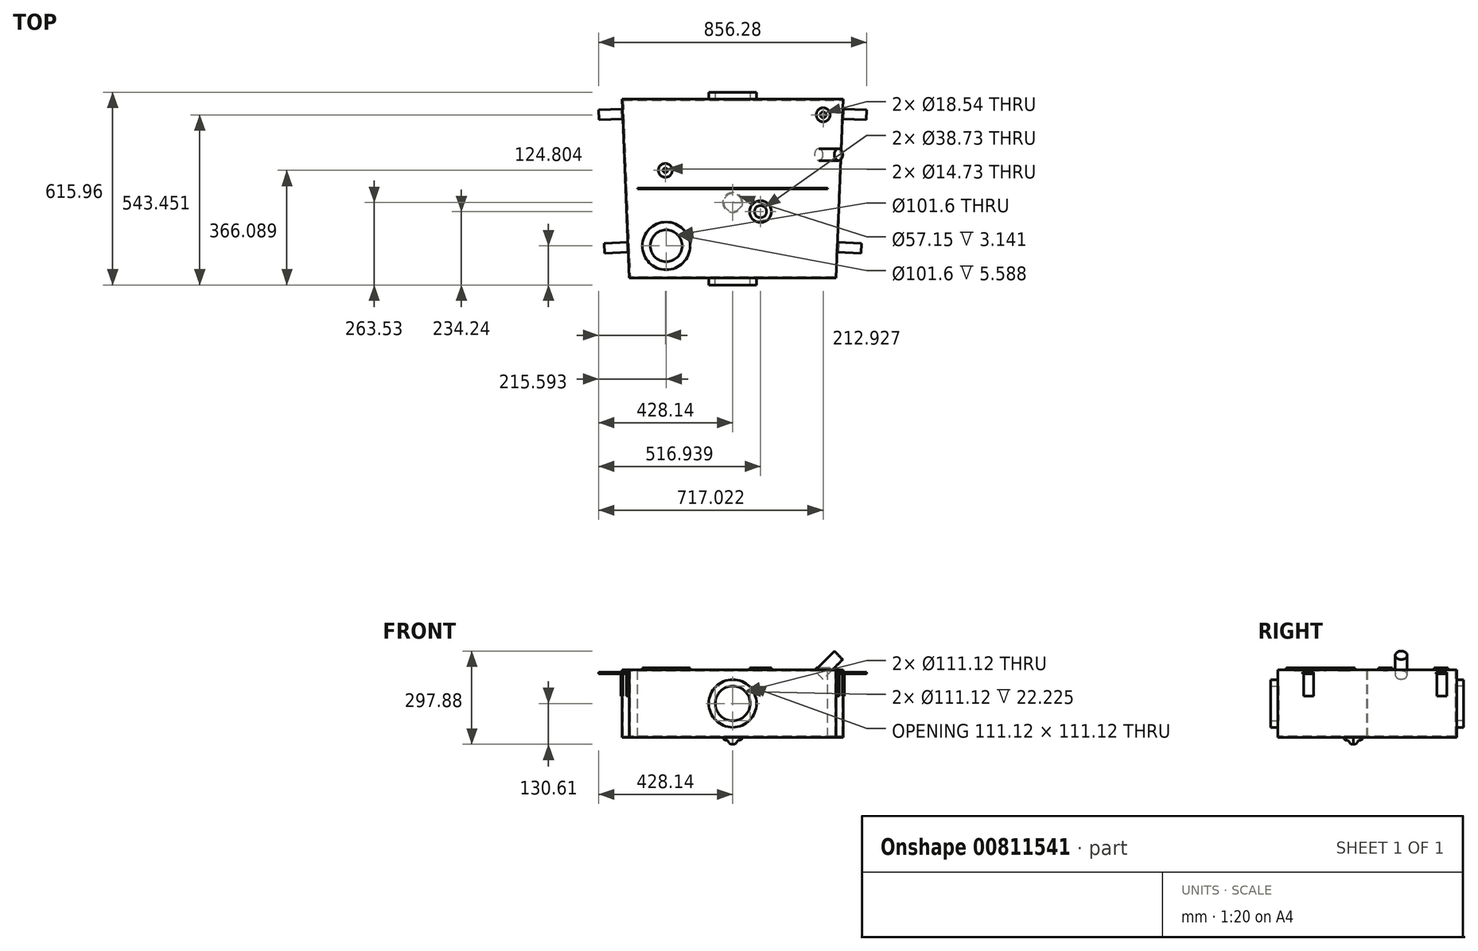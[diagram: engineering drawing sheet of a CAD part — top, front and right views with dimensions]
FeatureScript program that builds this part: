
annotation { "Feature Type Name" : "Feature", "Feature Type Description" : "" }
export const myFeature = defineFeature(function(context is Context, id is Id, definition is map)
    precondition{}
    {
        {
            var Q0;
            Q0=qCreatedBy(makeId("Top.planeOp"),FACE);
            var sketch = newSketch(context, id + "F0", { "sketchPlane" : qUnion([Q0])});
            skCircle(sketch, "E0", {"center": v(299.82, -177.22) * mm, "radius": 19.05 * mm});
            skCircle(sketch, "E1", {"center": v(288.88, -50.28) * mm, "radius": 9.27 * mm});
            skCircle(sketch, "E2", {"center": v(88.8, -359.5) * mm, "radius": 19.37 * mm});
            skCircle(sketch, "E3", {"center": v(88.8, -359.5) * mm, "radius": 34.93 * mm});
            skCircle(sketch, "E4", {"center": v(-212.55, -468.93) * mm, "radius": 76.2 * mm});
            skCircle(sketch, "E5", {"center": v(-212.55, -468.93) * mm, "radius": 50.8 * mm});
            skCircle(sketch, "E6", {"center": v(-215.21, -227.64) * mm, "radius": 22.23 * mm});
            skCircle(sketch, "E7", {"center": v(-215.21, -227.64) * mm, "radius": 7.37 * mm});
            skCircle(sketch, "E8", {"center": v(288.88, -50.28) * mm, "radius": 22.23 * mm});
            skLineSegment(sketch, "E9", {"start": v(0, -571.5) * mm, "end": v(330.2, -571.5) * mm});
            skLineSegment(sketch, "E10", {"start": v(0, 0) * mm, "end": v(353.29, 0) * mm});
            skLineSegment(sketch, "E11", {"start": v(353.29, 0) * mm, "end": v(330.2, -571.5) * mm});
            skLineSegment(sketch, "E12", {"start": v(356.77, -31.92) * mm, "end": v(352, -31.72) * mm});
            skLineSegment(sketch, "E13", {"start": v(356.77, -31.92) * mm, "end": v(355.48, -63.64) * mm});
            skLineSegment(sketch, "E14", {"start": v(355.48, -63.64) * mm, "end": v(350.73, -63.45) * mm});
            skLineSegment(sketch, "E15", {"start": v(338.3, -489.2) * mm, "end": v(333.53, -489.02) * mm});
            skLineSegment(sketch, "E16", {"start": v(338.3, -489.2) * mm, "end": v(339.57, -457.49) * mm});
            skLineSegment(sketch, "E17", {"start": v(339.57, -457.49) * mm, "end": v(334.81, -457.3) * mm});
            skLineSegment(sketch, "E18.MirrorCS", {"start": v(0, -571.5) * mm, "end": v(-330.2, -571.5) * mm});
            skLineSegment(sketch, "E19.MirrorCS", {"start": v(-353.29, 0) * mm, "end": v(-330.2, -571.5) * mm});
            skLineSegment(sketch, "E20.MirrorCS", {"start": v(0, 0) * mm, "end": v(-353.29, 0) * mm});
            skLineSegment(sketch, "E21.MirrorCS", {"start": v(-339.57, -457.49) * mm, "end": v(-334.81, -457.3) * mm});
            skLineSegment(sketch, "E22.MirrorCS", {"start": v(-338.3, -489.2) * mm, "end": v(-339.57, -457.49) * mm});
            skLineSegment(sketch, "E23.MirrorCS", {"start": v(-338.3, -489.2) * mm, "end": v(-333.53, -489.02) * mm});
            skLineSegment(sketch, "E24.MirrorCS", {"start": v(-356.77, -31.92) * mm, "end": v(-352, -31.72) * mm});
            skLineSegment(sketch, "E25.MirrorCS", {"start": v(-355.48, -63.64) * mm, "end": v(-350.73, -63.45) * mm});
            skLineSegment(sketch, "E26.MirrorCS", {"start": v(-356.77, -31.92) * mm, "end": v(-355.48, -63.64) * mm});
            skLineSegment(sketch, "E27", {"start": v(318.87, -177.28) * mm, "end": v(318.87, -145.64) * mm, "construction": true});
            skLineSegment(sketch, "E28", {"start": v(303.64, -284.16) * mm, "end": v(0, -284.16) * mm});
            skLineSegment(sketch, "E29", {"start": v(303.64, -287.34) * mm, "end": v(0, -287.34) * mm});
            skLineSegment(sketch, "E30", {"start": v(303.64, -284.16) * mm, "end": v(303.64, -287.34) * mm});
            skLineSegment(sketch, "E31.MirrorCS", {"start": v(-303.64, -284.16) * mm, "end": v(0, -284.16) * mm});
            skLineSegment(sketch, "E32.MirrorCS", {"start": v(-303.64, -287.34) * mm, "end": v(0, -287.34) * mm});
            skLineSegment(sketch, "E33.MirrorCS", {"start": v(-303.64, -284.16) * mm, "end": v(-303.64, -287.34) * mm});
            skLineSegment(sketch, "E34", {"start": v(318.87, -177.28) * mm, "end": v(280.77, -177.28) * mm, "construction": true});
            skLineSegment(sketch, "E35", {"start": v(-212.55, -468.93) * mm, "end": v(-215.21, -227.64) * mm, "construction": true});
            skSolve(sketch);
        }
        {
            var Q0;
            Q0=makeQuery(id+"F0.imprint","IMPRINT",FACE,{"disambiguationData":[TD([[makeQuery(id+"F0.imprint","IMPRINT",EDGE,{"derivedFrom":sQuery(id+"F0.wireOp",EDGE,"E0")}),-1.0]])]});
            var Q1;
            Q1=makeQuery(id+"F0.imprint","IMPRINT",FACE,{"disambiguationData":[TD([[makeQuery(id+"F0.imprint","IMPRINT",EDGE,{"derivedFrom":sQuery(id+"F0.wireOp",EDGE,"E6")}),1.0]])]});
            var Q2;
            Q2=makeQuery(id+"F0.imprint","IMPRINT",FACE,{"disambiguationData":[TD([[makeQuery(id+"F0.imprint","IMPRINT",EDGE,{"derivedFrom":sQuery(id+"F0.wireOp",EDGE,"E7")}),1.0]])]});
            var Q3;
            Q3=makeQuery(id+"F0.imprint","IMPRINT",FACE,{"disambiguationData":[TD([[makeQuery(id+"F0.imprint","IMPRINT",EDGE,{"derivedFrom":sQuery(id+"F0.wireOp",EDGE,"E4")}),1.0]])]});
            var Q4;
            Q4=makeQuery(id+"F0.imprint","IMPRINT",FACE,{"disambiguationData":[TD([[makeQuery(id+"F0.imprint","IMPRINT",EDGE,{"derivedFrom":sQuery(id+"F0.wireOp",EDGE,"E5")}),1.0]])]});
            var Q5;
            Q5=makeQuery(id+"F0.imprint","IMPRINT",FACE,{"disambiguationData":[TD([[makeQuery(id+"F0.imprint","IMPRINT",EDGE,{"derivedFrom":sQuery(id+"F0.wireOp",EDGE,"E28")}),1.0]])]});
            var Q6;
            Q6=makeQuery(id+"F0.imprint","IMPRINT",FACE,{"disambiguationData":[TD([[makeQuery(id+"F0.imprint","IMPRINT",EDGE,{"derivedFrom":sQuery(id+"F0.wireOp",EDGE,"E2")}),-1.0]])]});
            var Q7;
            Q7=makeQuery(id+"F0.imprint","IMPRINT",FACE,{"disambiguationData":[TD([[makeQuery(id+"F0.imprint","IMPRINT",EDGE,{"derivedFrom":sQuery(id+"F0.wireOp",EDGE,"E2")}),1.0]])]});
            var Q8;
            Q8=makeQuery(id+"F0.imprint","IMPRINT",FACE,{"disambiguationData":[TD([[makeQuery(id+"F0.imprint","IMPRINT",EDGE,{"derivedFrom":sQuery(id+"F0.wireOp",EDGE,"E0")}),1.0]])]});
            var Q9;
            Q9=makeQuery(id+"F0.imprint","IMPRINT",FACE,{"disambiguationData":[TD([[makeQuery(id+"F0.imprint","IMPRINT",EDGE,{"derivedFrom":sQuery(id+"F0.wireOp",EDGE,"E1")}),-1.0]])]});
            var Q10;
            Q10=makeQuery(id+"F0.imprint","IMPRINT",FACE,{"disambiguationData":[TD([[makeQuery(id+"F0.imprint","IMPRINT",EDGE,{"derivedFrom":sQuery(id+"F0.wireOp",EDGE,"E1")}),1.0]])]});
            extrude(context, id + "F1", {"entities" : qUnion([Q0, Q1, Q2, Q3, Q4, Q5, Q6, Q7, Q8, Q9, Q10]), "oppositeDirection" : true, "depth" : 215.9 * mm, "offsetDistance" : 25.4 * mm});
        }
        {
            var Q0;
            Q0=makeQuery(id+"F1.opExtrude","CAP_FACE",FACE,{"disambiguationData":[OSD([sQuery(id+"F0.wireOp",EDGE,"E9"),sQuery(id+"F0.wireOp",EDGE,"E10"),sQuery(id+"F0.wireOp",EDGE,"E11"),sQuery(id+"F0.wireOp",EDGE,"E18.MirrorCS"),sQuery(id+"F0.wireOp",EDGE,"E19.MirrorCS"),sQuery(id+"F0.wireOp",EDGE,"E20.MirrorCS")])],"isStart":true});
            var Q1;
            Q1=makeQuery(id+"F1.opExtrude","SWEPT_BODY",BODY,{"disambiguationData":[OSD([sQuery(id+"F0.wireOp",EDGE,"E9"),sQuery(id+"F0.wireOp",EDGE,"E10"),sQuery(id+"F0.wireOp",EDGE,"E11"),sQuery(id+"F0.wireOp",EDGE,"E18.MirrorCS"),sQuery(id+"F0.wireOp",EDGE,"E19.MirrorCS"),sQuery(id+"F0.wireOp",EDGE,"E20.MirrorCS")])]});
            shell(context, id + "F2", {"isHollow" : true, "entities" : qUnion([Q0]), "parts" : qUnion([Q1]), "thickness" : 3.17 * mm});
        }
        {
            var Q0;
            Q0=makeQuery(id+"F0.imprint","IMPRINT",FACE,{"disambiguationData":[TD([[makeQuery(id+"F0.imprint","IMPRINT",EDGE,{"derivedFrom":sQuery(id+"F0.wireOp",EDGE,"E28")}),1.0]])]});
            extrude(context, id + "F3", {"entities" : qUnion([Q0]), "oppositeDirection" : true, "depth" : 215.9 * mm, "offsetDistance" : 25.4 * mm});
        }
        {
            var Q0;
            Q0=makeQuery(id+"F0.imprint","IMPRINT",FACE,{"disambiguationData":[TD([[makeQuery(id+"F0.imprint","IMPRINT",EDGE,{"derivedFrom":sQuery(id+"F0.wireOp",EDGE,"E7")}),1.0]])]});
            var Q1;
            Q1=makeQuery(id+"F0.imprint","IMPRINT",FACE,{"disambiguationData":[TD([[makeQuery(id+"F0.imprint","IMPRINT",EDGE,{"derivedFrom":sQuery(id+"F0.wireOp",EDGE,"E5")}),1.0]])]});
            var Q2;
            Q2=makeQuery(id+"F0.imprint","IMPRINT",FACE,{"disambiguationData":[TD([[makeQuery(id+"F0.imprint","IMPRINT",EDGE,{"derivedFrom":sQuery(id+"F0.wireOp",EDGE,"E2")}),1.0]])]});
            var Q3;
            Q3=makeQuery(id+"F0.imprint","IMPRINT",FACE,{"disambiguationData":[TD([[makeQuery(id+"F0.imprint","IMPRINT",EDGE,{"derivedFrom":sQuery(id+"F0.wireOp",EDGE,"E1")}),1.0]])]});
            extrude(context, id + "F4", {"entities" : qUnion([Q0, Q1, Q2, Q3]), "operationType" : NewBodyOperationType.REMOVE, "oppositeDirection" : true, "depth" : 3.3 * mm, "offsetDistance" : 25.4 * mm});
        }
        {
            var Q0;
            Q0=makeQuery(id+"F0.imprint","IMPRINT",FACE,{"disambiguationData":[TD([[makeQuery(id+"F0.imprint","IMPRINT",EDGE,{"derivedFrom":sQuery(id+"F0.wireOp",EDGE,"E6")}),1.0]])]});
            var Q1;
            Q1=makeQuery(id+"F0.imprint","IMPRINT",FACE,{"disambiguationData":[TD([[makeQuery(id+"F0.imprint","IMPRINT",EDGE,{"derivedFrom":sQuery(id+"F0.wireOp",EDGE,"E4")}),1.0]])]});
            var Q2;
            Q2=makeQuery(id+"F0.imprint","IMPRINT",FACE,{"disambiguationData":[TD([[makeQuery(id+"F0.imprint","IMPRINT",EDGE,{"derivedFrom":sQuery(id+"F0.wireOp",EDGE,"E2")}),-1.0]])]});
            var Q3;
            Q3=makeQuery(id+"F0.imprint","IMPRINT",FACE,{"disambiguationData":[TD([[makeQuery(id+"F0.imprint","IMPRINT",EDGE,{"derivedFrom":sQuery(id+"F0.wireOp",EDGE,"E1")}),-1.0]])]});
            extrude(context, id + "F5", {"entities" : qUnion([Q0, Q1, Q2, Q3]), "depth" : 5.6 * mm, "offsetDistance" : 25.4 * mm});
        }
        {
            var Q0;
            Q0=makeQuery(id+"F1.opExtrude","SWEPT_FACE",FACE,{"disambiguationData":[OSD([sQuery(id+"F0.wireOp",EDGE,"E9"),sQuery(id+"F0.wireOp",EDGE,"E18.MirrorCS")])]});
            var sketch = newSketch(context, id + "F6", { "sketchPlane" : qUnion([Q0])});
            skCircle(sketch, "E36", {"center": v(0, -107.95) * mm, "radius": 76.2 * mm});
            skCircle(sketch, "E37", {"center": v(0, -107.95) * mm, "radius": 55.56 * mm});
            skSolve(sketch);
        }
        {
            var Q0;
            Q0=makeQuery(id+"F6.imprint","IMPRINT",FACE,{"disambiguationData":[TD([[makeQuery(id+"F6.imprint","IMPRINT",EDGE,{"derivedFrom":sQuery(id+"F6.wireOp",EDGE,"E37")}),1.0]])]});
            extrude(context, id + "F7", {"entities" : qUnion([Q0]), "operationType" : NewBodyOperationType.REMOVE, "oppositeDirection" : true, "depth" : 3.3 * mm, "offsetDistance" : 25.4 * mm});
        }
        {
            var Q0;
            Q0=makeQuery(id+"F6.imprint","IMPRINT",FACE,{"disambiguationData":[TD([[makeQuery(id+"F6.imprint","IMPRINT",EDGE,{"derivedFrom":sQuery(id+"F6.wireOp",EDGE,"E36")}),1.0]])]});
            extrude(context, id + "F8", {"entities" : qUnion([Q0]), "depth" : 22.22 * mm, "offsetDistance" : 25.4 * mm});
        }
        {
            var Q0;
            Q0=makeQuery(id+"F1.opExtrude","SWEPT_FACE",FACE,{"disambiguationData":[OSD([sQuery(id+"F0.wireOp",EDGE,"E10"),sQuery(id+"F0.wireOp",EDGE,"E20.MirrorCS")])]});
            var sketch = newSketch(context, id + "F9", { "sketchPlane" : qUnion([Q0])});
            skCircle(sketch, "E38", {"center": v(0, -107.95) * mm, "radius": 76.2 * mm});
            skCircle(sketch, "E39", {"center": v(0, -107.95) * mm, "radius": 55.56 * mm});
            skSolve(sketch);
        }
        {
            var Q0;
            Q0=makeQuery(id+"F9.imprint","IMPRINT",FACE,{"disambiguationData":[TD([[makeQuery(id+"F9.imprint","IMPRINT",EDGE,{"derivedFrom":sQuery(id+"F9.wireOp",EDGE,"E39")}),1.0]])]});
            extrude(context, id + "F10", {"entities" : qUnion([Q0]), "operationType" : NewBodyOperationType.REMOVE, "oppositeDirection" : true, "depth" : 3.3 * mm, "offsetDistance" : 25.4 * mm});
        }
        {
            var Q0;
            Q0=makeQuery(id+"F9.imprint","IMPRINT",FACE,{"disambiguationData":[TD([[makeQuery(id+"F9.imprint","IMPRINT",EDGE,{"derivedFrom":sQuery(id+"F9.wireOp",EDGE,"E38")}),1.0]])]});
            extrude(context, id + "F11", {"entities" : qUnion([Q0]), "depth" : 22.22 * mm, "offsetDistance" : 25.4 * mm});
        }
        {
            var Q0;
            Q0=makeQuery(id+"F1.opExtrude","CAP_FACE",FACE,{"disambiguationData":[OSD([sQuery(id+"F0.wireOp",EDGE,"E9"),sQuery(id+"F0.wireOp",EDGE,"E10"),sQuery(id+"F0.wireOp",EDGE,"E11"),sQuery(id+"F0.wireOp",EDGE,"E18.MirrorCS"),sQuery(id+"F0.wireOp",EDGE,"E19.MirrorCS"),sQuery(id+"F0.wireOp",EDGE,"E20.MirrorCS")])],"isStart":false});
            var sketch = newSketch(context, id + "F12", { "sketchPlane" : qUnion([Q0])});
            skLineSegment(sketch, "E40", {"start": v(0, 0) * mm, "end": v(0, 330.2) * mm, "construction": true});
            skCircle(sketch, "E41", {"center": v(0, 330.2) * mm, "radius": 28.58 * mm});
            skCircle(sketch, "E42", {"center": v(0, 330.2) * mm, "radius": 31.75 * mm});
            skSolve(sketch);
        }
        {
            var Q0;
            Q0=makeQuery(id+"F12.imprint","IMPRINT",FACE,{"disambiguationData":[TD([[makeQuery(id+"F12.imprint","IMPRINT",EDGE,{"derivedFrom":sQuery(id+"F12.wireOp",EDGE,"E41")}),1.0]])]});
            extrude(context, id + "F13", {"entities" : qUnion([Q0]), "operationType" : NewBodyOperationType.REMOVE, "oppositeDirection" : true, "depth" : 3.3 * mm, "offsetDistance" : 25.4 * mm});
        }
        {
            var Q0;
            Q0=qCreatedBy(makeId("Front.planeOp"),FACE);
            cPlane(context, id + "F14", {"entities" : qUnion([Q0]), "cplaneType" : CPlaneType.OFFSET, "offset" : 330.2 * mm, "width" : 152.4 * mm, "height" : 152.4 * mm});
        }
        {
            var Q0;
            Q0=qCreatedBy(id+"F14.planeOp",FACE);
            var sketch = newSketch(context, id + "F15", { "sketchPlane" : qUnion([Q0])});
            skLineSegment(sketch, "E43", {"start": v(0, -215.87) * mm, "end": v(31.74, -215.87) * mm});
            skLineSegment(sketch, "E44", {"start": v(0, -215.87) * mm, "end": v(0, -238.1) * mm});
            skFitSpline(sketch, "E45", {"points": [v(0, -238.1) * mm, v(6.54, -238.1) * mm, v(12.33, -232.24) * mm, v(18.56, -225.83) * mm, v(25.6, -224.58) * mm, v(31.74, -215.87) * mm], "startDerivative": vector(38.6, -6.75) * mm, "endDerivative": vector(23.38, 49.2) * mm});
            skSolve(sketch);
        }
        {
            var Q0;
            Q0=makeQuery(id+"F15.imprint","IMPRINT",FACE,{"disambiguationData":[TD([[makeQuery(id+"F15.imprint","IMPRINT",EDGE,{"derivedFrom":sQuery(id+"F15.wireOp",EDGE,"E43")}),-1.0]])]});
            extrude(context, id + "F16", {"entities" : qUnion([Q0]), "depth" : 0.25 * mm, "offsetDistance" : 25.4 * mm});
        }
        {
            var Q0;
            Q0=makeQuery(id+"F16.opExtrude","CAP_FACE",FACE,{"disambiguationData":[OSD([sQuery(id+"F15.wireOp",EDGE,"E43"),sQuery(id+"F15.wireOp",EDGE,"E44"),sQuery(id+"F15.wireOp",EDGE,"E45")])],"isStart":false});
            var Q1;
            Q1=makeQuery(id+"F16.opExtrude","CAP_EDGE",EDGE,{"disambiguationData":[OSD([sQuery(id+"F15.wireOp",EDGE,"E44")])],"isStart":true});
            revolve(context, id + "F17", {"operationType" : NewBodyOperationType.ADD, "surfaceOperationType" : NewSurfaceOperationType.NEW, "entities" : qUnion([Q0]), "axis" : qUnion([Q1]), "revolveType" : RevolveType.FULL});
        }
        {
            var Q0;
            {var subQ0=sQuery(id+"F0.wireOp",EDGE,"E24.MirrorCS");Q0=makeQuery(id+"F0.imprint","IMPRINT",FACE,{"disambiguationData":[TD([[makeQuery(id+"F0.imprint","IMPRINT",EDGE,{"derivedFrom":subQ0}),-1.0]])]});}
            var Q1;
            {var subQ0=sQuery(id+"F0.wireOp",EDGE,"E12");Q1=makeQuery(id+"F0.imprint","IMPRINT",FACE,{"disambiguationData":[TD([[makeQuery(id+"F0.imprint","IMPRINT",EDGE,{"derivedFrom":subQ0}),1.0]])]});}
            var Q2;
            {var subQ0=sQuery(id+"F0.wireOp",EDGE,"E15");Q2=makeQuery(id+"F0.imprint","IMPRINT",FACE,{"disambiguationData":[TD([[makeQuery(id+"F0.imprint","IMPRINT",EDGE,{"derivedFrom":subQ0}),-1.0]])]});}
            var Q3;
            {var subQ0=sQuery(id+"F0.wireOp",EDGE,"E21.MirrorCS");Q3=makeQuery(id+"F0.imprint","IMPRINT",FACE,{"disambiguationData":[TD([[makeQuery(id+"F0.imprint","IMPRINT",EDGE,{"derivedFrom":subQ0}),-1.0]])]});}
            extrude(context, id + "F18", {"entities" : qUnion([Q0, Q1, Q2, Q3]), "oppositeDirection" : true, "depth" : 84.14 * mm, "offsetDistance" : 25.4 * mm});
        }
        {
            var Q0;
            {var subQ0=sQuery(id+"F0.wireOp",EDGE,"E24.MirrorCS");Q0=makeQuery(id+"F0.imprint","IMPRINT",FACE,{"disambiguationData":[TD([[makeQuery(id+"F0.imprint","IMPRINT",EDGE,{"derivedFrom":subQ0}),-1.0]])]});}
            var Q1;
            {var subQ0=sQuery(id+"F0.wireOp",EDGE,"E12");Q1=makeQuery(id+"F0.imprint","IMPRINT",FACE,{"disambiguationData":[TD([[makeQuery(id+"F0.imprint","IMPRINT",EDGE,{"derivedFrom":subQ0}),1.0]])]});}
            var Q2;
            {var subQ0=sQuery(id+"F0.wireOp",EDGE,"E15");Q2=makeQuery(id+"F0.imprint","IMPRINT",FACE,{"disambiguationData":[TD([[makeQuery(id+"F0.imprint","IMPRINT",EDGE,{"derivedFrom":subQ0}),-1.0]])]});}
            var Q3;
            {var subQ0=sQuery(id+"F0.wireOp",EDGE,"E21.MirrorCS");Q3=makeQuery(id+"F0.imprint","IMPRINT",FACE,{"disambiguationData":[TD([[makeQuery(id+"F0.imprint","IMPRINT",EDGE,{"derivedFrom":subQ0}),-1.0]])]});}
            extrude(context, id + "F19", {"entities" : qUnion([Q0, Q1, Q2, Q3]), "operationType" : NewBodyOperationType.REMOVE, "oppositeDirection" : true, "depth" : 7.94 * mm, "offsetDistance" : 25.4 * mm});
        }
        {
            var Q0;
            Q0=makeQuery(id+"F18.opExtrude","SWEPT_FACE",FACE,{"disambiguationData":[OSD([sQuery(id+"F0.wireOp",EDGE,"E26.MirrorCS")])]});
            var sketch = newSketch(context, id + "F20", { "sketchPlane" : qUnion([Q0])});
            skLineSegment(sketch, "E46", {"start": v(17.49, -7.94) * mm, "end": v(17.49, -12.7) * mm});
            skLineSegment(sketch, "E47", {"start": v(17.49, -12.7) * mm, "end": v(49.24, -12.7) * mm});
            skLineSegment(sketch, "E48", {"start": v(49.24, -12.7) * mm, "end": v(49.24, -7.94) * mm});
            skLineSegment(sketch, "E49", {"start": v(49.24, -7.94) * mm, "end": v(17.49, -7.94) * mm});
            skSolve(sketch);
        }
        {
            var Q0;
            Q0=makeQuery(id+"F20.imprint","IMPRINT",FACE,{"disambiguationData":[TD([[makeQuery(id+"F20.imprint","IMPRINT",EDGE,{"derivedFrom":sQuery(id+"F20.wireOp",EDGE,"E46")}),-1.0]])]});
            extrude(context, id + "F21", {"entities" : qUnion([Q0]), "operationType" : NewBodyOperationType.ADD, "depth" : 71.44 * mm, "offsetDistance" : 25.4 * mm});
        }
        {
            var Q0;
            Q0=makeQuery(id+"F18.opExtrude","SWEPT_FACE",FACE,{"disambiguationData":[OSD([sQuery(id+"F0.wireOp",EDGE,"E22.MirrorCS")])]});
            var sketch = newSketch(context, id + "F22", { "sketchPlane" : qUnion([Q0])});
            skLineSegment(sketch, "E50", {"start": v(443.4, -7.94) * mm, "end": v(443.4, -12.7) * mm});
            skLineSegment(sketch, "E51", {"start": v(443.4, -12.7) * mm, "end": v(475.15, -12.7) * mm});
            skLineSegment(sketch, "E52", {"start": v(475.15, -12.7) * mm, "end": v(475.15, -7.94) * mm});
            skLineSegment(sketch, "E53", {"start": v(475.15, -7.94) * mm, "end": v(443.4, -7.94) * mm});
            skSolve(sketch);
        }
        {
            var Q0;
            Q0=makeQuery(id+"F22.imprint","IMPRINT",FACE,{"disambiguationData":[TD([[makeQuery(id+"F22.imprint","IMPRINT",EDGE,{"derivedFrom":sQuery(id+"F22.wireOp",EDGE,"E50")}),-1.0]])]});
            extrude(context, id + "F23", {"entities" : qUnion([Q0]), "operationType" : NewBodyOperationType.ADD, "depth" : 71.44 * mm, "offsetDistance" : 25.4 * mm});
        }
        {
            var Q0;
            Q0=makeQuery(id+"F18.opExtrude","SWEPT_FACE",FACE,{"disambiguationData":[OSD([sQuery(id+"F0.wireOp",EDGE,"E16")])]});
            var sketch = newSketch(context, id + "F24", { "sketchPlane" : qUnion([Q0])});
            skLineSegment(sketch, "E54", {"start": v(-475.15, -7.94) * mm, "end": v(-475.15, -12.7) * mm});
            skLineSegment(sketch, "E55", {"start": v(-475.15, -12.7) * mm, "end": v(-443.4, -12.7) * mm});
            skLineSegment(sketch, "E56", {"start": v(-443.4, -12.7) * mm, "end": v(-443.4, -7.94) * mm});
            skLineSegment(sketch, "E57", {"start": v(-443.4, -7.94) * mm, "end": v(-475.15, -7.94) * mm});
            skSolve(sketch);
        }
        {
            var Q0;
            Q0=makeQuery(id+"F24.imprint","IMPRINT",FACE,{"disambiguationData":[TD([[makeQuery(id+"F24.imprint","IMPRINT",EDGE,{"derivedFrom":sQuery(id+"F24.wireOp",EDGE,"E54")}),-1.0]])]});
            extrude(context, id + "F25", {"entities" : qUnion([Q0]), "operationType" : NewBodyOperationType.ADD, "depth" : 71.44 * mm, "offsetDistance" : 25.4 * mm});
        }
        {
            var Q0;
            Q0=makeQuery(id+"F18.opExtrude","SWEPT_FACE",FACE,{"disambiguationData":[OSD([sQuery(id+"F0.wireOp",EDGE,"E13")])]});
            var sketch = newSketch(context, id + "F26", { "sketchPlane" : qUnion([Q0])});
            skLineSegment(sketch, "E58", {"start": v(-49.24, -7.94) * mm, "end": v(-49.24, -12.7) * mm});
            skLineSegment(sketch, "E59", {"start": v(-49.24, -12.7) * mm, "end": v(-17.49, -12.7) * mm});
            skLineSegment(sketch, "E60", {"start": v(-17.49, -12.7) * mm, "end": v(-17.49, -7.94) * mm});
            skLineSegment(sketch, "E61", {"start": v(-17.49, -7.94) * mm, "end": v(-49.24, -7.94) * mm});
            skSolve(sketch);
        }
        {
            var Q0;
            Q0=makeQuery(id+"F26.imprint","IMPRINT",FACE,{"disambiguationData":[TD([[makeQuery(id+"F26.imprint","IMPRINT",EDGE,{"derivedFrom":sQuery(id+"F26.wireOp",EDGE,"E58")}),-1.0]])]});
            extrude(context, id + "F27", {"entities" : qUnion([Q0]), "operationType" : NewBodyOperationType.ADD, "depth" : 71.44 * mm, "offsetDistance" : 25.4 * mm});
        }
        {
            var Q0;
            Q0=makeQuery(id+"F0.imprint","IMPRINT",FACE,{"disambiguationData":[TD([[makeQuery(id+"F0.imprint","IMPRINT",EDGE,{"derivedFrom":sQuery(id+"F0.wireOp",EDGE,"E0")}),1.0]])]});
            extrude(context, id + "F28", {"entities" : qUnion([Q0]), "depth" : 88.9 * mm, "offsetDistance" : 25.4 * mm});
        }
        {
            var Q0;
            Q0=makeQuery(id+"F28.opExtrude","SWEPT_BODY",BODY,{"disambiguationData":[OSD([sQuery(id+"F0.wireOp",EDGE,"E0")])]});
            var Q1;
            Q1=sQuery(id+"F0.wireOp",EDGE,"E27");
            transform(context, id + "F29", {"entities" : qUnion([Q0]), "transformType" : TransformType.ROTATION, "transformAxis" : qUnion([Q1]), "angle" : 45 * degree, "makeCopy" : false});
        }
        {
            var Q0;
            Q0=makeQuery(id+"F28.opExtrude","SWEPT_BODY",BODY,{"disambiguationData":[OSD([sQuery(id+"F0.wireOp",EDGE,"E0")])]});
            transform(context, id + "F30", {"entities" : qUnion([Q0]), "transformType" : TransformType.TRANSLATION_3D, "dx" : -30.48 * mm, "dy" : 0 * mm, "dz" : -30.48 * mm, "makeCopy" : false});
        }
    });
